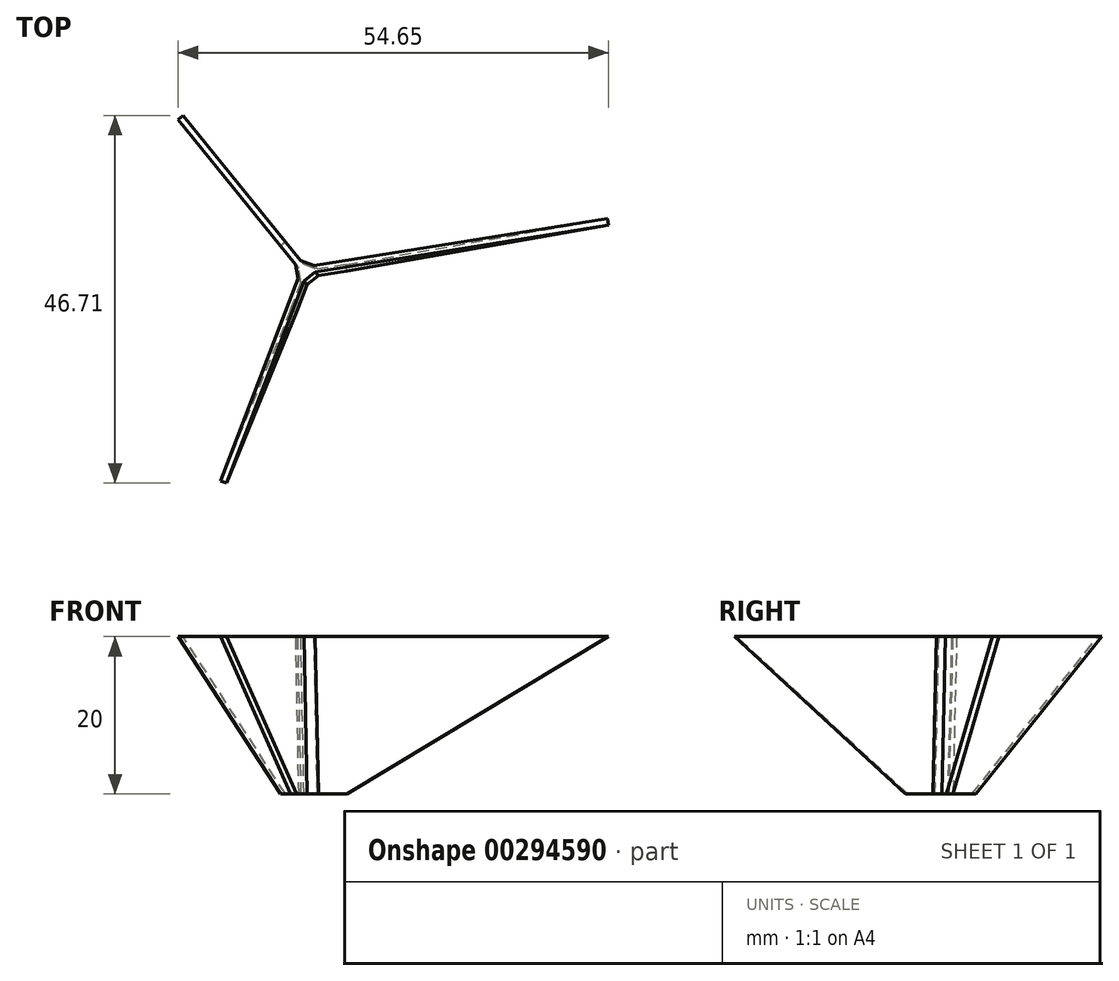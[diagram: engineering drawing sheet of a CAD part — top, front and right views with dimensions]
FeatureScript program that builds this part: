
annotation { "Feature Type Name" : "Feature", "Feature Type Description" : "" }
export const myFeature = defineFeature(function(context is Context, id is Id, definition is map)
    precondition{}
    {
        {
            var Q0;
            Q0=qCreatedBy(makeId("Top.planeOp"),FACE);
            var sketch = newSketch(context, id + "F0", { "sketchPlane" : qUnion([Q0])});
            skCircle(sketch, "E0.cCircle", {"center": v(0, 0) * mm, "radius": 1 * mm, "construction": true});
            skLineSegment(sketch, "E0.0", {"start": v(1.97, 0.32) * mm, "end": v(1.34, -0.2) * mm, "construction": true});
            skLineSegment(sketch, "E0.1", {"start": v(-0.71, -1.87) * mm, "end": v(-0.84, -1.06) * mm, "construction": true});
            skLineSegment(sketch, "E0.2", {"start": v(-1.26, 1.55) * mm, "end": v(-1.26, 1.55) * mm});
            skPoint(sketch, "E0.0.midPoint", {"position": v(0.63, -0.78) * mm});
            skLineSegment(sketch, "E1", {"start": v(4.94, 0.79) * mm, "end": v(1.97, 0.32) * mm, "construction": true});
            skLineSegment(sketch, "E2", {"start": v(-1.79, -4.67) * mm, "end": v(-0.71, -1.87) * mm, "construction": true});
            skLineSegment(sketch, "E3", {"start": v(0, 0) * mm, "end": v(-1.26, 1.55) * mm, "construction": true});
            skLineSegment(sketch, "E4", {"start": v(1.97, 0.32) * mm, "end": v(0, 0) * mm, "construction": true});
            skLineSegment(sketch, "E5", {"start": v(-1.26, 1.55) * mm, "end": v(-0.5, 1.26) * mm, "construction": true});
            skLineSegment(sketch, "E6", {"start": v(-1.26, 1.55) * mm, "end": v(-3.15, 3.88) * mm, "construction": true});
            skLineSegment(sketch, "E7", {"start": v(-0.71, -1.87) * mm, "end": v(0, 0) * mm, "construction": true});
            skLineSegment(sketch, "E8.0", {"start": v(-1.13, 0.74) * mm, "end": v(-3.47, 3.62) * mm});
            skLineSegment(sketch, "E9.0", {"start": v(-0.5, 1.26) * mm, "end": v(-2.83, 4.14) * mm});
            skLineSegment(sketch, "E10.0", {"start": v(-1.4, -4.82) * mm, "end": v(-0.08, -1.35) * mm});
            skLineSegment(sketch, "E11.0", {"start": v(-2.17, -4.52) * mm, "end": v(-0.84, -1.06) * mm});
            skLineSegment(sketch, "E12.0", {"start": v(5, 0.38) * mm, "end": v(1.34, -0.2) * mm});
            skLineSegment(sketch, "E13.0", {"start": v(4.87, 1.2) * mm, "end": v(1.2, 0.6) * mm});
            skLineSegment(sketch, "E14", {"start": v(-3.47, 3.62) * mm, "end": v(-2.83, 4.14) * mm});
            skLineSegment(sketch, "E15", {"start": v(-2.17, -4.52) * mm, "end": v(-1.4, -4.82) * mm});
            skLineSegment(sketch, "E16", {"start": v(5, 0.38) * mm, "end": v(4.87, 1.2) * mm});
            skLineSegment(sketch, "E17", {"start": v(-0.84, -1.06) * mm, "end": v(-1.13, 0.74) * mm});
            skLineSegment(sketch, "E18", {"start": v(-0.08, -1.35) * mm, "end": v(-0.71, -1.87) * mm, "construction": true});
            skLineSegment(sketch, "E19", {"start": v(-0.5, 1.26) * mm, "end": v(1.2, 0.6) * mm});
            skLineSegment(sketch, "E20", {"start": v(-1.13, 0.74) * mm, "end": v(-1.26, 1.55) * mm, "construction": true});
            skLineSegment(sketch, "E21", {"start": v(1.2, 0.6) * mm, "end": v(1.97, 0.32) * mm, "construction": true});
            skLineSegment(sketch, "E22", {"start": v(1.34, -0.2) * mm, "end": v(-0.08, -1.35) * mm});
            skSolve(sketch);
        }
        {
            var Q0;
            Q0=qCreatedBy(makeId("Top.planeOp"),FACE);
            cPlane(context, id + "F1", {"entities" : qUnion([Q0]), "cplaneType" : CPlaneType.OFFSET, "offset" : 20 * mm, "width" : 150 * mm, "height" : 150 * mm});
        }
        {
            var Q0;
            Q0=qCreatedBy(id+"F1.planeOp",FACE);
            var sketch = newSketch(context, id + "F2", { "sketchPlane" : qUnion([Q0])});
            skCircle(sketch, "E23.cCircle", {"center": v(-0.4, 0.49) * mm, "radius": 1 * mm, "construction": true});
            skLineSegment(sketch, "E23.0", {"start": v(1.58, 0.8) * mm, "end": v(0.94, 0.28) * mm, "construction": true});
            skLineSegment(sketch, "E23.1", {"start": v(-1.1, -1.38) * mm, "end": v(-1.24, -0.57) * mm, "construction": true});
            skLineSegment(sketch, "E23.2", {"start": v(-1.65, 2.04) * mm, "end": v(-1.65, 2.04) * mm});
            skPoint(sketch, "E23.0.midPoint", {"position": v(0.24, -0.3) * mm});
            skLineSegment(sketch, "E24", {"start": v(38.12, 6.63) * mm, "end": v(1.58, 0.8) * mm, "construction": true});
            skLineSegment(sketch, "E25", {"start": v(-10.68, -26.41) * mm, "end": v(-1.1, -1.38) * mm, "construction": true});
            skLineSegment(sketch, "E26", {"start": v(-0.4, 0.49) * mm, "end": v(-1.65, 2.04) * mm, "construction": true});
            skLineSegment(sketch, "E27", {"start": v(1.58, 0.8) * mm, "end": v(-0.4, 0.49) * mm, "construction": true});
            skLineSegment(sketch, "E28", {"start": v(-1.65, 2.04) * mm, "end": v(-0.89, 1.75) * mm, "construction": true});
            skLineSegment(sketch, "E29", {"start": v(-1.65, 2.04) * mm, "end": v(-16.15, 19.9) * mm, "construction": true});
            skLineSegment(sketch, "E30", {"start": v(-1.1, -1.38) * mm, "end": v(-0.4, 0.49) * mm, "construction": true});
            skLineSegment(sketch, "E31.0", {"start": v(-1.53, 1.23) * mm, "end": v(-16.47, 19.64) * mm});
            skLineSegment(sketch, "E32.0", {"start": v(-0.89, 1.75) * mm, "end": v(-15.83, 20.15) * mm});
            skLineSegment(sketch, "E33.0", {"start": v(-10.3, -26.56) * mm, "end": v(-0.47, -0.87) * mm});
            skLineSegment(sketch, "E34.0", {"start": v(-11.07, -26.27) * mm, "end": v(-1.24, -0.57) * mm});
            skLineSegment(sketch, "E35.0", {"start": v(38.18, 6.23) * mm, "end": v(0.94, 0.28) * mm});
            skLineSegment(sketch, "E36.0", {"start": v(38.05, 7.04) * mm, "end": v(0.82, 1.1) * mm});
            skLineSegment(sketch, "E37", {"start": v(-16.47, 19.64) * mm, "end": v(-15.83, 20.15) * mm});
            skLineSegment(sketch, "E38", {"start": v(-11.07, -26.27) * mm, "end": v(-10.3, -26.56) * mm});
            skLineSegment(sketch, "E39", {"start": v(38.18, 6.23) * mm, "end": v(38.05, 7.04) * mm});
            skLineSegment(sketch, "E40", {"start": v(-1.24, -0.57) * mm, "end": v(-1.53, 1.23) * mm});
            skLineSegment(sketch, "E41", {"start": v(-0.47, -0.87) * mm, "end": v(-1.1, -1.38) * mm, "construction": true});
            skLineSegment(sketch, "E42", {"start": v(-0.89, 1.75) * mm, "end": v(0.82, 1.1) * mm});
            skLineSegment(sketch, "E43", {"start": v(-1.53, 1.23) * mm, "end": v(-1.65, 2.04) * mm, "construction": true});
            skLineSegment(sketch, "E44", {"start": v(0.82, 1.1) * mm, "end": v(1.58, 0.8) * mm, "construction": true});
            skLineSegment(sketch, "E45", {"start": v(0.94, 0.28) * mm, "end": v(-0.47, -0.87) * mm});
            skSolve(sketch);
        }
        {
            var Q0;
            Q0 = qSketchRegion(id + "F0", true);
            var Q1;
            Q1 = qSketchRegion(id + "F2", true);
            loft(context, id + "F3", {"sheetProfilesArray" : [{ "sheetProfileEntities" : qUnion([Q0]) }, { "sheetProfileEntities" : qUnion([Q1]) }]});
        }
    });
